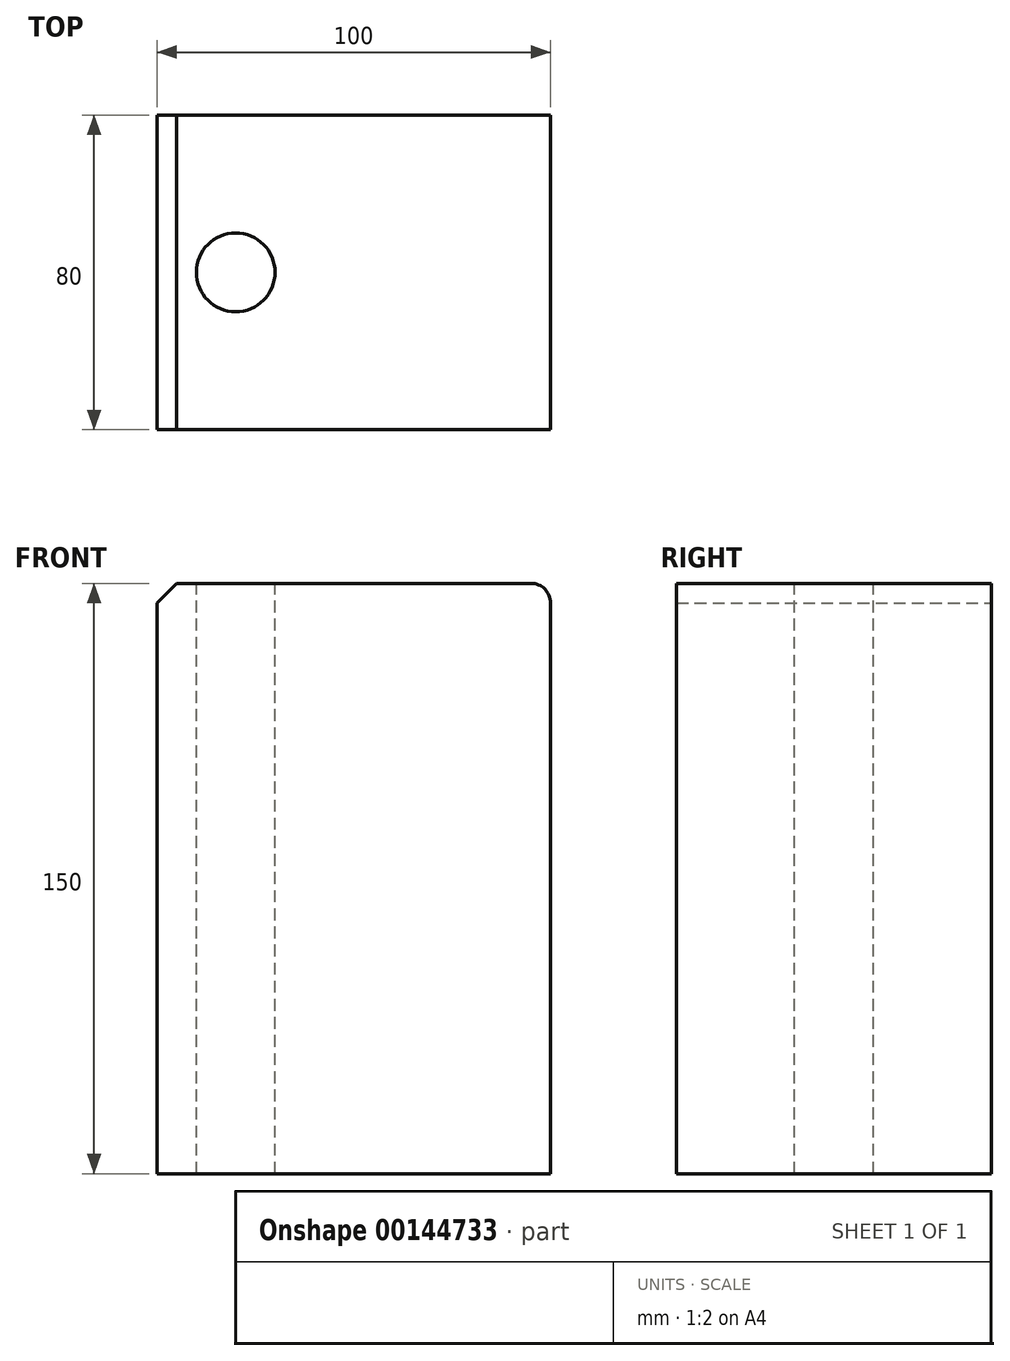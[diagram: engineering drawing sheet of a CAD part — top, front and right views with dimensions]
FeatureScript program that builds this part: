
annotation { "Feature Type Name" : "Feature", "Feature Type Description" : "" }
export const myFeature = defineFeature(function(context is Context, id is Id, definition is map)
    precondition{}
    {
        {
            var Q0;
            Q0=qCreatedBy(makeId("Front.planeOp"),FACE);
            var sketch = newSketch(context, id + "F0", { "sketchPlane" : qUnion([Q0])});
            skLineSegment(sketch, "E0.bottom", {"start": v(50, 75) * mm, "end": v(-50, 75) * mm});
            skLineSegment(sketch, "E0.top", {"start": v(50, -75) * mm, "end": v(-50, -75) * mm});
            skLineSegment(sketch, "E0.left", {"start": v(50, 75) * mm, "end": v(50, -75) * mm});
            skLineSegment(sketch, "E0.right", {"start": v(-50, 75) * mm, "end": v(-50, -75) * mm});
            skPoint(sketch, "E0.middle", {"position": v(0, 0) * mm});
            skSolve(sketch);
        }
        {
            var Q0;
            Q0 = qSketchRegion(id + "F0", true);
            extrude(context, id + "F1", {"entities" : qUnion([Q0]), "endBound" : BoundingType.SYMMETRIC, "depth" : 80 * mm});
        }
        {
            var Q0;
            Q0=makeQuery(id+"F1.opExtrude","SWEPT_FACE",FACE,{"disambiguationData":[OSD([sQuery(id+"F0.wireOp",EDGE,"E0.bottom")])]});
            var sketch = newSketch(context, id + "F2", { "sketchPlane" : qUnion([Q0])});
            skCircle(sketch, "E1", {"center": v(-30, 0) * mm, "radius": 5 * mm});
            skSolve(sketch);
        }
        {
            var Q0;
            Q0=sQuery(id+"F2.wireOp",VERTEX,"E1.center");
            var Q1;
            Q1=makeQuery(id+"F1.opExtrude","SWEPT_BODY",BODY,{"disambiguationData":[OSD([sQuery(id+"F0.wireOp",EDGE,"E0.bottom"),sQuery(id+"F0.wireOp",EDGE,"E0.top"),sQuery(id+"F0.wireOp",EDGE,"E0.left"),sQuery(id+"F0.wireOp",EDGE,"E0.right")])]});
            hole(context, id + "F3", {"style" : HoleStyle.SIMPLE, "endStyle" : HoleEndStyle.THROUGH, "standardTappedOrClearance" : lookupTablePath({ "standard" : "ISO", "size" : "20", "type" : "Drilled" }), "standardBlindInLast" : lookupTablePath({ "standard" : "ISO", "size" : "20", "type" : "Drilled" }), "holeDiameter" : 20 * mm, "locations" : qUnion([Q0]), "scope" : qUnion([Q1]), "isTappedThrough" : true});
        }
        {
            var Q0;
            Q0=makeQuery(id+"F1.opExtrude","SWEPT_EDGE",EDGE,{"disambiguationData":[OSD([sQuery(id+"F0.wireOp",EDGE,"E0.bottom"),sQuery(id+"F0.wireOp",EDGE,"E0.right")])]});
            chamfer(context, id + "F4", {"entities" : qUnion([Q0]), "width" : 5 * mm, "tangentPropagation" : true});
        }
        {
            var Q0;
            Q0=makeQuery(id+"F1.opExtrude","SWEPT_EDGE",EDGE,{"disambiguationData":[OSD([sQuery(id+"F0.wireOp",EDGE,"E0.bottom"),sQuery(id+"F0.wireOp",EDGE,"E0.left")])]});
            fillet(context, id + "F5", {"entities" : qUnion([Q0]), "radius" : 5 * mm, "tangentPropagation" : true, "allowEdgeOverflow" : false});
        }
    });
